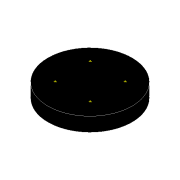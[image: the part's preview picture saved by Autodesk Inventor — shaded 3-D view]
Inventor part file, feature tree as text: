
AUTODESK INVENTOR PART (.ipt)
format: ipt  version: 2022 (Build 260153000, 153)  size: 85,504 bytes
history: native  units: mm
features: sketch x4, extrude x1
ambient origin geometry x8: Origin, YZ Plane, XZ Plane, XY Plane, X Axis, Y Axis, Z Axis, Center Point
bodies: Solid1 (feature_tree)
feature tree (5):
  extrude  "Extrusion1"  Depth=1.0mm TaperAngle=0.0deg
  sketch  "Sketch2"  dims[d3=2.5mm]
  sketch  "Sketch3"  dims[d4=2.5mm]
  sketch  "Sketch4"
  sketch  "Sketch1"  dims[d0=6.0mm d1=1.0mm d2=0.0mm]
